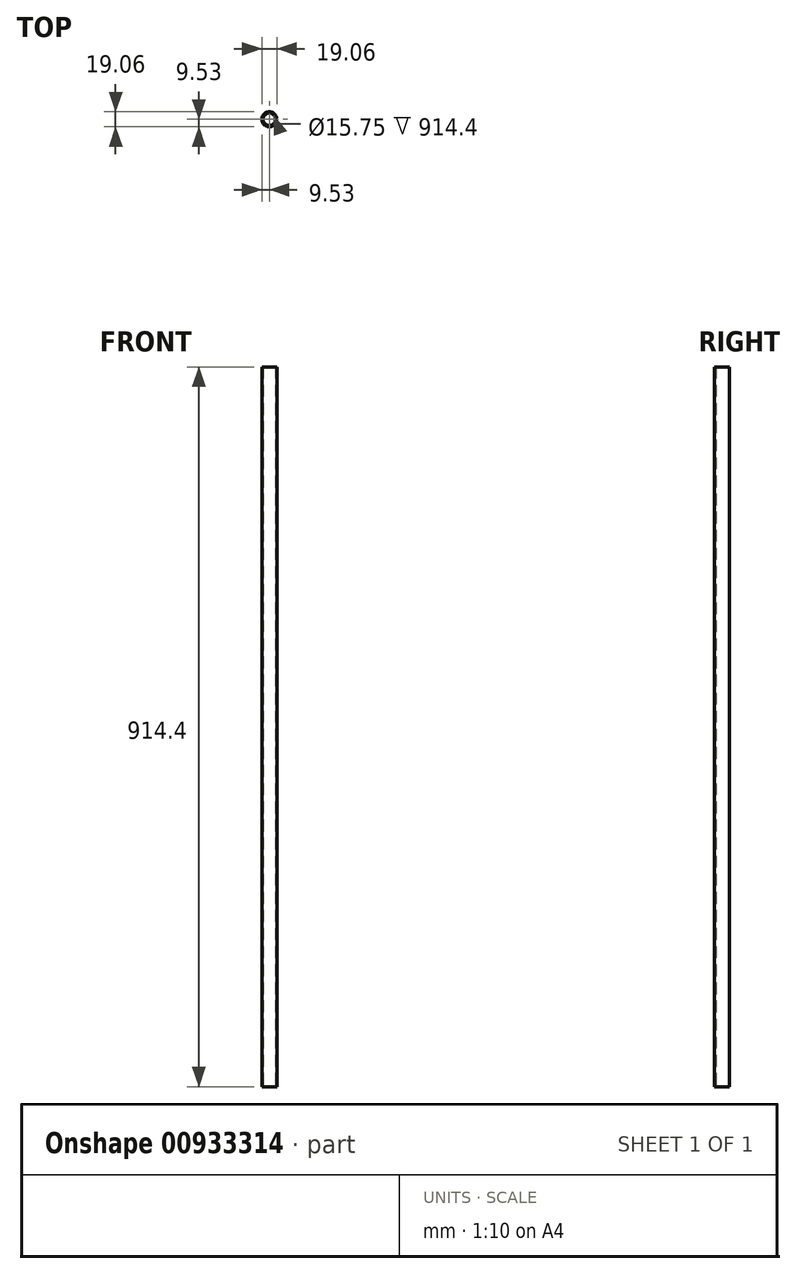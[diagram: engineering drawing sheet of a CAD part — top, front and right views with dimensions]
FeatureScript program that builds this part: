
annotation { "Feature Type Name" : "Feature", "Feature Type Description" : "" }
export const myFeature = defineFeature(function(context is Context, id is Id, definition is map)
    precondition{}
    {
        {
            var Q0;
            Q0=qCreatedBy(makeId("Top.planeOp"),FACE);
            var sketch = newSketch(context, id + "F0", { "sketchPlane" : qUnion([Q0])});
            skCircle(sketch, "E0", {"center": v(0, 0) * mm, "radius": 9.53 * mm});
            skCircle(sketch, "E1", {"center": v(0, 0) * mm, "radius": 7.87 * mm});
            skSolve(sketch);
        }
        {
            var Q0;
            Q0=makeQuery(id+"F0.imprint","IMPRINT",FACE,{"disambiguationData":[TD([[makeQuery(id+"F0.imprint","IMPRINT",EDGE,{"derivedFrom":sQuery(id+"F0.wireOp",EDGE,"E0")}),1.0]])]});
            extrude(context, id + "F1", {"entities" : qUnion([Q0]), "depth" : 914.4 * mm, "offsetDistance" : 25.4 * mm});
        }
    });
